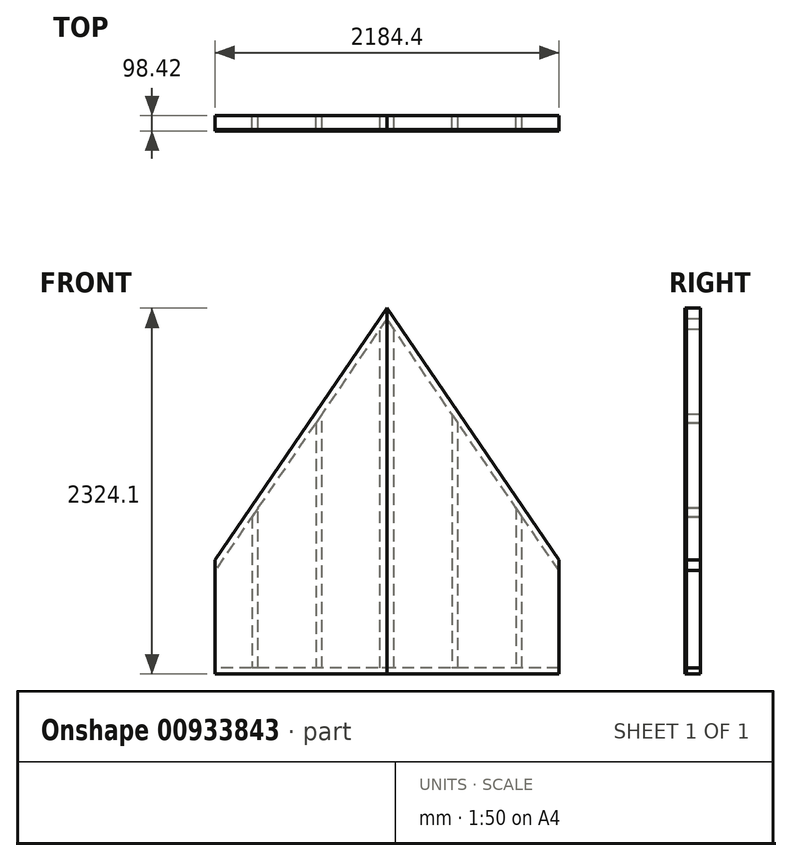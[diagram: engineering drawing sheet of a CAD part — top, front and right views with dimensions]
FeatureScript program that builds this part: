
annotation { "Feature Type Name" : "Feature", "Feature Type Description" : "" }
export const myFeature = defineFeature(function(context is Context, id is Id, definition is map)
    precondition{}
    {
        {
            var Q0;
            Q0=qCreatedBy(makeId("Front.planeOp"),FACE);
            var sketch = newSketch(context, id + "F0", { "sketchPlane" : qUnion([Q0])});
            skLineSegment(sketch, "E0.bottom", {"start": v(1093.7, 19.05) * mm, "end": v(-1090.7, 19.05) * mm});
            skLineSegment(sketch, "E0.top", {"start": v(1093.7, -19.05) * mm, "end": v(-1090.7, -19.05) * mm});
            skLineSegment(sketch, "E0.left", {"start": v(1093.7, 19.05) * mm, "end": v(1093.7, -19.05) * mm});
            skLineSegment(sketch, "E0.right", {"start": v(-1090.7, 19.05) * mm, "end": v(-1090.7, -19.05) * mm});
            skPoint(sketch, "E0.middle", {"position": v(1.5, 0) * mm});
            skLineSegment(sketch, "E1.bottom", {"start": v(-1052.6, 19.05) * mm, "end": v(-1090.7, 19.05) * mm});
            skLineSegment(sketch, "E1.top", {"start": v(-1052.6, 704.85) * mm, "end": v(-1090.7, 704.85) * mm});
            skLineSegment(sketch, "E1.left", {"start": v(-1052.6, 19.05) * mm, "end": v(-1052.6, 704.85) * mm});
            skLineSegment(sketch, "E1.right", {"start": v(-1090.7, 19.05) * mm, "end": v(-1090.7, 704.85) * mm});
            skLineSegment(sketch, "E2.bottom", {"start": v(1093.7, 19.05) * mm, "end": v(1055.6, 19.05) * mm});
            skLineSegment(sketch, "E2.top", {"start": v(1093.7, 704.85) * mm, "end": v(1055.6, 704.85) * mm});
            skLineSegment(sketch, "E2.left", {"start": v(1093.7, 19.05) * mm, "end": v(1093.7, 704.85) * mm});
            skLineSegment(sketch, "E2.right", {"start": v(1055.6, 19.05) * mm, "end": v(1055.6, 704.85) * mm});
            skLineSegment(sketch, "E3", {"start": v(0, 19.05) * mm, "end": v(0, 2305.05) * mm, "construction": true});
            skLineSegment(sketch, "E4", {"start": v(0, 2305.05) * mm, "end": v(-1090.7, 704.85) * mm});
            skLineSegment(sketch, "E5", {"start": v(0, 2305.05) * mm, "end": v(1093.7, 704.85) * mm});
            skLineSegment(sketch, "E6", {"start": v(-1329.77, 286.46) * mm, "end": v(304, 2683.4) * mm, "construction": true});
            skLineSegment(sketch, "E7", {"start": v(-467.14, 2921) * mm, "end": v(1790.23, -381.76) * mm, "construction": true});
            skLineSegment(sketch, "E8", {"start": v(0, 2305.05) * mm, "end": v(0, 2237.53) * mm});
            skLineSegment(sketch, "E9", {"start": v(0, 2237.53) * mm, "end": v(-1090.7, 637.33) * mm});
            skLineSegment(sketch, "E10", {"start": v(-1090.7, 637.33) * mm, "end": v(-1090.7, 704.85) * mm});
            skLineSegment(sketch, "E11", {"start": v(1093.7, 704.85) * mm, "end": v(1093.7, 637.33) * mm});
            skLineSegment(sketch, "E12", {"start": v(1093.7, 637.33) * mm, "end": v(0, 2237.53) * mm});
            skLineSegment(sketch, "E13", {"start": v(44.45, 19.05) * mm, "end": v(44.45, 2172.5) * mm});
            skLineSegment(sketch, "E14", {"start": v(-44.45, 19.05) * mm, "end": v(-44.45, 2172.32) * mm});
            skLineSegment(sketch, "E15", {"start": v(-44.45, 2172.32) * mm, "end": v(0, 2237.53) * mm});
            skLineSegment(sketch, "E16", {"start": v(44.45, 2172.5) * mm, "end": v(0, 2237.53) * mm});
            skLineSegment(sketch, "E17.bottom", {"start": v(-857.25, 1590.18) * mm, "end": v(-819.15, 1590.18) * mm, "construction": true});
            skLineSegment(sketch, "E17.top", {"start": v(-857.25, -304.06) * mm, "end": v(-819.15, -304.06) * mm, "construction": true});
            skLineSegment(sketch, "E17.left", {"start": v(-857.25, 1590.18) * mm, "end": v(-857.25, -304.06) * mm, "construction": true});
            skLineSegment(sketch, "E17.right", {"start": v(-819.15, 1590.18) * mm, "end": v(-819.15, -304.06) * mm, "construction": true});
            skLineSegment(sketch, "E18.bottom", {"start": v(-450.85, 2029.32) * mm, "end": v(-412.75, 2029.32) * mm, "construction": true});
            skLineSegment(sketch, "E18.top", {"start": v(-450.85, -671.1) * mm, "end": v(-412.75, -671.1) * mm, "construction": true});
            skLineSegment(sketch, "E18.left", {"start": v(-450.85, 2029.32) * mm, "end": v(-450.85, -671.1) * mm, "construction": true});
            skLineSegment(sketch, "E18.right", {"start": v(-412.75, 2029.32) * mm, "end": v(-412.75, -671.1) * mm, "construction": true});
            skLineSegment(sketch, "E19.bottom", {"start": v(450.85, 2357.04) * mm, "end": v(412.75, 2357.04) * mm, "construction": true});
            skLineSegment(sketch, "E19.top", {"start": v(450.85, -638.33) * mm, "end": v(412.75, -638.33) * mm, "construction": true});
            skLineSegment(sketch, "E19.left", {"start": v(450.85, 2357.04) * mm, "end": v(450.85, -638.33) * mm, "construction": true});
            skLineSegment(sketch, "E19.right", {"start": v(412.75, 2357.04) * mm, "end": v(412.75, -638.33) * mm, "construction": true});
            skLineSegment(sketch, "E20.bottom", {"start": v(857.25, 1701.6) * mm, "end": v(819.15, 1701.6) * mm, "construction": true});
            skLineSegment(sketch, "E20.top", {"start": v(857.25, -749.76) * mm, "end": v(819.15, -749.76) * mm, "construction": true});
            skLineSegment(sketch, "E20.left", {"start": v(857.25, 1701.6) * mm, "end": v(857.25, -749.76) * mm, "construction": true});
            skLineSegment(sketch, "E20.right", {"start": v(819.15, 1701.6) * mm, "end": v(819.15, -749.76) * mm, "construction": true});
            skLineSegment(sketch, "E21", {"start": v(-857.25, 979.83) * mm, "end": v(-857.25, 19.05) * mm});
            skLineSegment(sketch, "E22", {"start": v(-857.25, 19.05) * mm, "end": v(-819.15, 19.05) * mm});
            skPoint(sketch, "E22.endSnap0", {"position": v(-819.15, 643.06) * mm});
            skLineSegment(sketch, "E23", {"start": v(-819.15, 19.05) * mm, "end": v(-819.15, 1035.6) * mm});
            skLineSegment(sketch, "E24", {"start": v(-819.15, 1035.6) * mm, "end": v(-857.25, 979.83) * mm});
            skLineSegment(sketch, "E25", {"start": v(-450.85, 1576.07) * mm, "end": v(-450.85, 19.05) * mm});
            skLineSegment(sketch, "E26", {"start": v(-450.85, 19.05) * mm, "end": v(-412.75, 19.05) * mm});
            skLineSegment(sketch, "E27", {"start": v(-412.75, 19.05) * mm, "end": v(-412.75, 1631.97) * mm});
            skLineSegment(sketch, "E28", {"start": v(-412.75, 1631.97) * mm, "end": v(-450.85, 1576.07) * mm});
            skLineSegment(sketch, "E29", {"start": v(412.75, 1633.63) * mm, "end": v(412.75, 19.05) * mm});
            skLineSegment(sketch, "E30", {"start": v(412.75, 19.05) * mm, "end": v(450.85, 19.05) * mm});
            skLineSegment(sketch, "E31", {"start": v(450.85, 19.05) * mm, "end": v(450.85, 1577.89) * mm});
            skLineSegment(sketch, "E32", {"start": v(450.85, 1577.89) * mm, "end": v(412.75, 1633.63) * mm});
            skLineSegment(sketch, "E33", {"start": v(819.15, 1039.03) * mm, "end": v(819.15, 19.05) * mm});
            skLineSegment(sketch, "E34", {"start": v(819.15, 19.05) * mm, "end": v(857.25, 19.05) * mm});
            skLineSegment(sketch, "E35", {"start": v(857.25, 19.05) * mm, "end": v(857.25, 983.28) * mm});
            skLineSegment(sketch, "E36", {"start": v(857.25, 983.28) * mm, "end": v(819.15, 1039.03) * mm});
            skSolve(sketch);
        }
        {
            var Q0;
            {var subQ0=sQuery(id+"F0.wireOp",EDGE,"E1.bottom");Q0=makeQuery(id+"F0.imprint","IMPRINT",FACE,{"disambiguationData":[TD([[makeQuery(id+"F0.imprint","IMPRINT",EDGE,{"derivedFrom":subQ0}),-1.0]])]});}
            var Q1;
            Q1=makeQuery(id+"F0.imprint","IMPRINT",FACE,{"disambiguationData":[TD([[makeQuery(id+"F0.imprint","IMPRINT",EDGE,{"derivedFrom":sQuery(id+"F0.wireOp",EDGE,"E21")}),1.0]])]});
            var Q2;
            Q2=makeQuery(id+"F0.imprint","IMPRINT",FACE,{"disambiguationData":[TD([[makeQuery(id+"F0.imprint","IMPRINT",EDGE,{"derivedFrom":sQuery(id+"F0.wireOp",EDGE,"E25")}),1.0]])]});
            var Q3;
            {var subQ1=sQuery(id+"F0.wireOp",EDGE,"E13");Q3=makeQuery(id+"F0.imprint","IMPRINT",FACE,{"disambiguationData":[TD([[makeQuery(id+"F0.imprint","IMPRINT",EDGE,{"derivedFrom":subQ1}),1.0]])]});}
            var Q4;
            Q4=makeQuery(id+"F0.imprint","IMPRINT",FACE,{"disambiguationData":[TD([[makeQuery(id+"F0.imprint","IMPRINT",EDGE,{"derivedFrom":sQuery(id+"F0.wireOp",EDGE,"E29")}),1.0]])]});
            var Q5;
            Q5=makeQuery(id+"F0.imprint","IMPRINT",FACE,{"disambiguationData":[TD([[makeQuery(id+"F0.imprint","IMPRINT",EDGE,{"derivedFrom":sQuery(id+"F0.wireOp",EDGE,"E33")}),1.0]])]});
            var Q6;
            {var subQ0=sQuery(id+"F0.wireOp",EDGE,"E2.bottom");Q6=makeQuery(id+"F0.imprint","IMPRINT",FACE,{"disambiguationData":[TD([[makeQuery(id+"F0.imprint","IMPRINT",EDGE,{"derivedFrom":subQ0}),-1.0]])]});}
            extrude(context, id + "F1", {"entities" : qUnion([Q0, Q1, Q2, Q3, Q4, Q5, Q6]), "depth" : 88.9 * mm, "offsetDistance" : 25.4 * mm});
        }
        {
            var Q0;
            {var subQ0=sQuery(id+"F0.wireOp",EDGE,"E1.top");Q0=makeQuery(id+"F0.imprint","IMPRINT",FACE,{"disambiguationData":[TD([[makeQuery(id+"F0.imprint","IMPRINT",EDGE,{"derivedFrom":subQ0}),-1.0]])]});}
            var Q1;
            Q1=makeQuery(id+"F0.imprint","IMPRINT",FACE,{"disambiguationData":[TD([[makeQuery(id+"F0.imprint","IMPRINT",EDGE,{"derivedFrom":sQuery(id+"F0.wireOp",EDGE,"E0.top")}),-1.0]])]});
            var Q2;
            {var subQ0=sQuery(id+"F0.wireOp",EDGE,"E1.top");Q2=makeQuery(id+"F0.imprint","IMPRINT",FACE,{"disambiguationData":[TD([[makeQuery(id+"F0.imprint","IMPRINT",EDGE,{"derivedFrom":subQ0}),1.0]])]});}
            extrude(context, id + "F2", {"entities" : qUnion([Q0, Q1, Q2]), "depth" : 88.9 * mm, "offsetDistance" : 25.4 * mm});
        }
        {
            var Q0;
            {var subQ1=sQuery(id+"F0.wireOp",EDGE,"E2.top");Q0=makeQuery(id+"F0.imprint","IMPRINT",FACE,{"disambiguationData":[TD([[makeQuery(id+"F0.imprint","IMPRINT",EDGE,{"derivedFrom":subQ1}),-1.0]])]});}
            var Q1;
            {var subQ0=sQuery(id+"F0.wireOp",EDGE,"E2.top");Q1=makeQuery(id+"F0.imprint","IMPRINT",FACE,{"disambiguationData":[TD([[makeQuery(id+"F0.imprint","IMPRINT",EDGE,{"derivedFrom":subQ0}),1.0]])]});}
            extrude(context, id + "F3", {"entities" : qUnion([Q0, Q1]), "depth" : 88.9 * mm, "offsetDistance" : 25.4 * mm});
        }
        {
            var Q0;
            Q0=makeQuery(id+"F1.opExtrude","CAP_FACE",FACE,{"disambiguationData":[OSD([sQuery(id+"F0.wireOp",EDGE,"E0.bottom"),sQuery(id+"F0.wireOp",EDGE,"E13"),sQuery(id+"F0.wireOp",EDGE,"E14"),sQuery(id+"F0.wireOp",EDGE,"E15"),sQuery(id+"F0.wireOp",EDGE,"E16")])],"isStart":false});
            var sketch = newSketch(context, id + "F4", { "sketchPlane" : qUnion([Q0])});
            skLineSegment(sketch, "E37.0", {"start": v(0, 2305.05) * mm, "end": v(-1090.7, 704.85) * mm});
            skLineSegment(sketch, "E38.0", {"start": v(0, 2305.05) * mm, "end": v(1093.7, 704.85) * mm});
            skLineSegment(sketch, "E39.0", {"start": v(1093.7, 19.05) * mm, "end": v(1093.7, 637.33) * mm});
            skLineSegment(sketch, "E40.0", {"start": v(1093.7, -19.05) * mm, "end": v(-1090.7, -19.05) * mm});
            skLineSegment(sketch, "E41.0", {"start": v(1093.7, 19.05) * mm, "end": v(1093.7, -19.05) * mm});
            skLineSegment(sketch, "E42.0", {"start": v(-1090.7, 19.05) * mm, "end": v(-1090.7, 637.33) * mm});
            skLineSegment(sketch, "E43.0", {"start": v(-1090.7, 19.05) * mm, "end": v(-1090.7, -19.05) * mm});
            skLineSegment(sketch, "E44", {"start": v(0, 2305.05) * mm, "end": v(0, -19.05) * mm});
            skPoint(sketch, "E44.endSnap0", {"position": v(0, 19.05) * mm});
            skLineSegment(sketch, "E45.0", {"start": v(-1090.7, 637.33) * mm, "end": v(-1090.7, 704.85) * mm});
            skPoint(sketch, "E46.0", {"position": v(1093.7, 704.85) * mm});
            skLineSegment(sketch, "E47.0", {"start": v(1093.7, 704.85) * mm, "end": v(1093.7, 637.33) * mm});
            skSolve(sketch);
        }
        {
            var Q0;
            {var subQ8=sQuery(id+"F4.wireOp",EDGE,"E37.0");Q0=makeQuery(id+"F4.imprint","IMPRINT",FACE,{"disambiguationData":[TD([[makeQuery(id+"F4.imprint","IMPRINT",EDGE,{"derivedFrom":subQ8}),1.0]])]});}
            var Q1;
            {var subQ4=makeQuery(id+"F1.opExtrude","CAP_EDGE",EDGE,{"disambiguationData":[OSD([sQuery(id+"F0.wireOp",EDGE,"E14")])],"isStart":false});Q1=makeQuery(id+"F4.imprint","IMPRINT",FACE,{"disambiguationData":[TD([[makeQuery(id+"F4.imprint","IMPRINT",EDGE,{"derivedFrom":subQ4}),-1.0]])]});}
            extrude(context, id + "F5", {"entities" : qUnion([Q0, Q1]), "depth" : 9.52 * mm, "offsetDistance" : 25.4 * mm});
        }
        {
            var Q0;
            {var subQ6=sQuery(id+"F4.wireOp",EDGE,"E38.0");Q0=makeQuery(id+"F4.imprint","IMPRINT",FACE,{"disambiguationData":[TD([[makeQuery(id+"F4.imprint","IMPRINT",EDGE,{"derivedFrom":subQ6}),-1.0]])]});}
            var Q1;
            {var subQ4=makeQuery(id+"F1.opExtrude","CAP_EDGE",EDGE,{"disambiguationData":[OSD([sQuery(id+"F0.wireOp",EDGE,"E13")])],"isStart":false});Q1=makeQuery(id+"F4.imprint","IMPRINT",FACE,{"disambiguationData":[TD([[makeQuery(id+"F4.imprint","IMPRINT",EDGE,{"derivedFrom":subQ4}),1.0]])]});}
            extrude(context, id + "F6", {"entities" : qUnion([Q0, Q1]), "depth" : 9.52 * mm, "offsetDistance" : 25.4 * mm});
        }
    });
